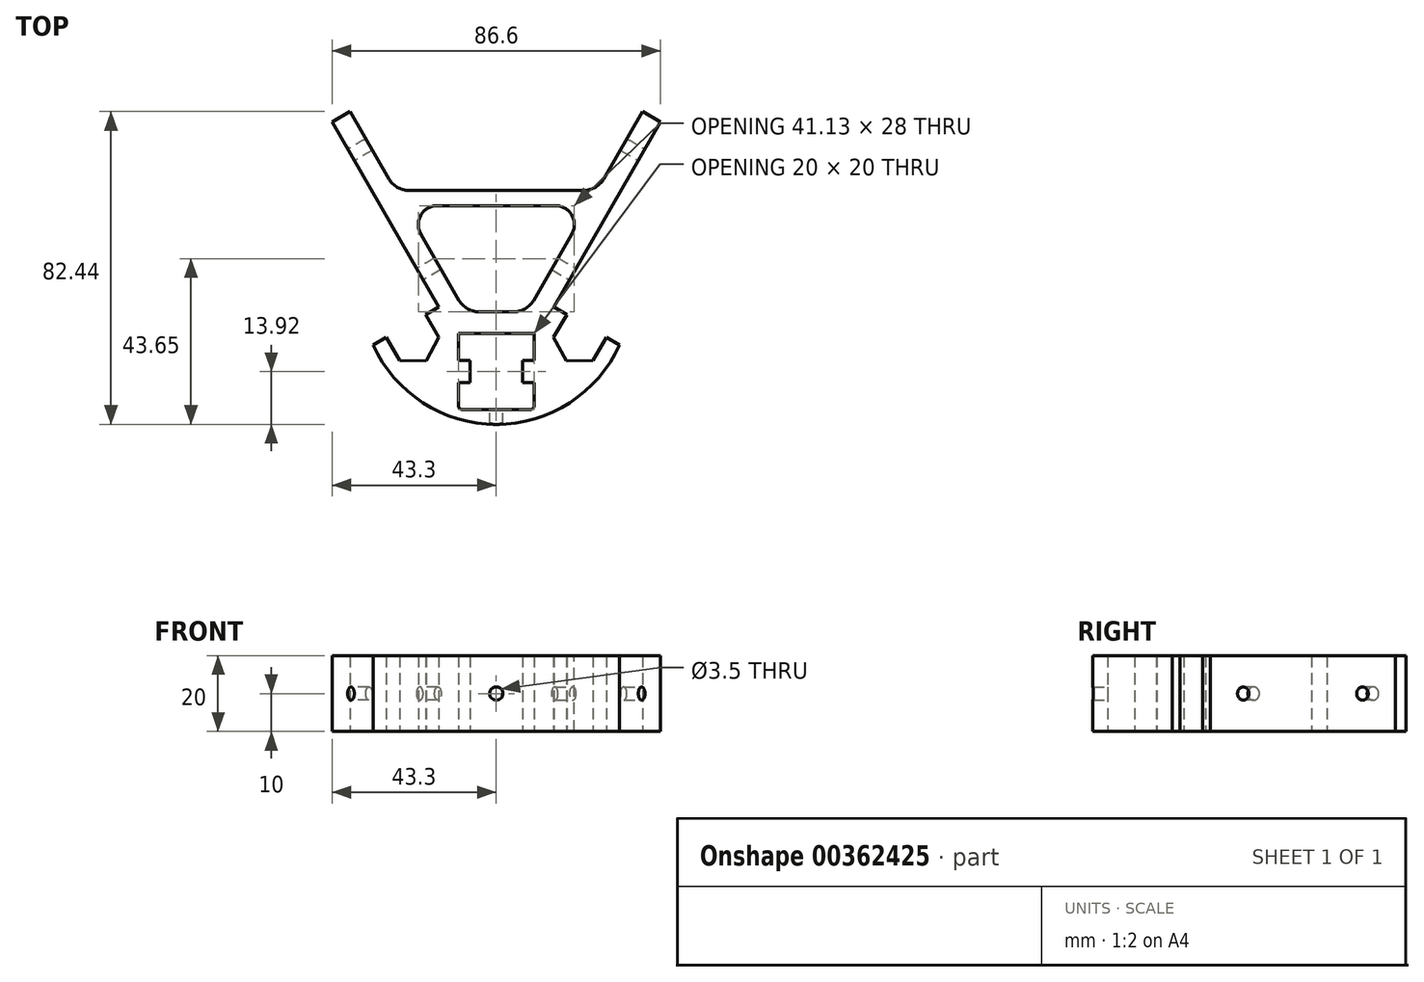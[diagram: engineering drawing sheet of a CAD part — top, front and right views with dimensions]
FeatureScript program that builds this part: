
annotation { "Feature Type Name" : "Feature", "Feature Type Description" : "" }
export const myFeature = defineFeature(function(context is Context, id is Id, definition is map)
    precondition{}
    {
        {
            var Q0;
            Q0=qCreatedBy(makeId("Top.planeOp"),FACE);
            var sketch = newSketch(context, id + "F0", { "sketchPlane" : qUnion([Q0])});
            skLineSegment(sketch, "E0", {"start": v(0, 0) * mm, "end": v(32.48, 0) * mm});
            skLineSegment(sketch, "E1", {"start": v(0, 0) * mm, "end": v(-32.48, 0) * mm});
            skArc(sketch, "E2", {"start": v(-32.48, 0) * mm, "mid": v(0, -20.94) * mm, "end": v(32.48, 0) * mm});
            skLineSegment(sketch, "E3", {"start": v(-32.48, 0) * mm, "end": v(-15.15, 10) * mm});
            skLineSegment(sketch, "E4", {"start": v(32.48, 0) * mm, "end": v(15.15, 10) * mm});
            skLineSegment(sketch, "E5", {"start": v(15.15, 10) * mm, "end": v(43.3, 58.75) * mm});
            skLineSegment(sketch, "E6", {"start": v(-15.15, 10) * mm, "end": v(-43.3, 58.75) * mm});
            skLineSegment(sketch, "E7", {"start": v(38.54, 61.5) * mm, "end": v(43.3, 58.75) * mm});
            skLineSegment(sketch, "E8.bottom", {"start": v(10, -17.02) * mm, "end": v(-10, -17.02) * mm});
            skLineSegment(sketch, "E8.top", {"start": v(10, 2.98) * mm, "end": v(-10, 2.98) * mm});
            skLineSegment(sketch, "E8.left", {"start": v(10, -17.02) * mm, "end": v(10, 2.98) * mm});
            skLineSegment(sketch, "E8.right", {"start": v(-10, -17.02) * mm, "end": v(-10, 2.98) * mm});
            skPoint(sketch, "E8.middle", {"position": v(0, -7.02) * mm});
            skLineSegment(sketch, "E9", {"start": v(-98.14, 8.7) * mm, "end": v(40.87, 8.7) * mm});
            skLineSegment(sketch, "E10", {"start": v(-43.3, 58.75) * mm, "end": v(-38.54, 61.5) * mm});
            skLineSegment(sketch, "E11", {"start": v(-38.54, 61.5) * mm, "end": v(-8.06, 8.7) * mm});
            skLineSegment(sketch, "E12", {"start": v(38.54, 61.5) * mm, "end": v(8.06, 8.7) * mm});
            skLineSegment(sketch, "E13", {"start": v(-98.14, 36.7) * mm, "end": v(34.35, 36.7) * mm});
            skLineSegment(sketch, "E14", {"start": v(-98.39, 40.7) * mm, "end": v(36.56, 40.7) * mm});
            skLineSegment(sketch, "E15.bottom", {"start": v(-10, -7.02) * mm, "end": v(-6.9, -7.02) * mm});
            skLineSegment(sketch, "E15.top", {"start": v(-10, -4.12) * mm, "end": v(-6.9, -4.12) * mm});
            skLineSegment(sketch, "E15.left", {"start": v(-10, -7.02) * mm, "end": v(-10, -4.12) * mm});
            skLineSegment(sketch, "E15.right", {"start": v(-6.9, -7.02) * mm, "end": v(-6.9, -4.12) * mm});
            skLineSegment(sketch, "E16.top", {"start": v(-10, -9.92) * mm, "end": v(-6.9, -9.92) * mm});
            skLineSegment(sketch, "E16.left", {"start": v(-10, -7.02) * mm, "end": v(-10, -9.92) * mm});
            skLineSegment(sketch, "E16.right", {"start": v(-6.9, -7.02) * mm, "end": v(-6.9, -9.92) * mm});
            skLineSegment(sketch, "E17.1.0", {"start": v(10, 2.98) * mm, "end": v(10, -17.02) * mm});
            skLineSegment(sketch, "E17.1.1", {"start": v(2.9, -17.02) * mm, "end": v(2.9, -13.92) * mm});
            skLineSegment(sketch, "E17.1.2", {"start": v(0, -17.02) * mm, "end": v(0, -13.92) * mm});
            skLineSegment(sketch, "E17.1.3", {"start": v(-2.9, -17.02) * mm, "end": v(-2.9, -13.92) * mm});
            skLineSegment(sketch, "E17.1.4", {"start": v(0, -13.92) * mm, "end": v(-2.9, -13.92) * mm});
            skLineSegment(sketch, "E17.1.5", {"start": v(0, -13.92) * mm, "end": v(2.9, -13.92) * mm});
            skLineSegment(sketch, "E17.2.0", {"start": v(-10, 2.98) * mm, "end": v(10, 2.98) * mm});
            skLineSegment(sketch, "E17.2.1", {"start": v(10, -4.12) * mm, "end": v(6.9, -4.12) * mm});
            skLineSegment(sketch, "E17.2.2", {"start": v(10, -7.02) * mm, "end": v(6.9, -7.02) * mm});
            skLineSegment(sketch, "E17.2.3", {"start": v(10, -9.92) * mm, "end": v(6.9, -9.92) * mm});
            skLineSegment(sketch, "E17.2.4", {"start": v(6.9, -7.02) * mm, "end": v(6.9, -9.92) * mm});
            skLineSegment(sketch, "E17.2.5", {"start": v(6.9, -7.02) * mm, "end": v(6.9, -4.12) * mm});
            skLineSegment(sketch, "E17.3.1", {"start": v(-2.9, 2.98) * mm, "end": v(-2.9, -0.12) * mm});
            skLineSegment(sketch, "E17.3.2", {"start": v(0, 2.98) * mm, "end": v(0, -0.12) * mm});
            skLineSegment(sketch, "E17.3.3", {"start": v(2.9, 2.98) * mm, "end": v(2.9, -0.12) * mm});
            skLineSegment(sketch, "E17.3.4", {"start": v(0, -0.12) * mm, "end": v(2.9, -0.12) * mm});
            skLineSegment(sketch, "E17.3.5", {"start": v(0, -0.12) * mm, "end": v(-2.9, -0.12) * mm});
            skLineSegment(sketch, "E18", {"start": v(18.62, 8) * mm, "end": v(15.12, 1.94) * mm});
            skLineSegment(sketch, "E19", {"start": v(29.01, 2) * mm, "end": v(25.51, -4.06) * mm});
            skPoint(sketch, "E20", {"position": v(23.81, 5) * mm});
            skLineSegment(sketch, "E21", {"start": v(15.12, 1.94) * mm, "end": v(18.51, -4.18) * mm});
            skLineSegment(sketch, "E22", {"start": v(25.51, -4.06) * mm, "end": v(18.51, -4.18) * mm});
            skLineSegment(sketch, "E23.MirrorCS", {"start": v(-18.62, 8) * mm, "end": v(-15.12, 1.94) * mm});
            skLineSegment(sketch, "E24.MirrorCS", {"start": v(-15.12, 1.94) * mm, "end": v(-18.51, -4.18) * mm});
            skLineSegment(sketch, "E25.MirrorCS", {"start": v(-25.51, -4.06) * mm, "end": v(-18.51, -4.18) * mm});
            skLineSegment(sketch, "E26.MirrorCS", {"start": v(-29.01, 2) * mm, "end": v(-25.51, -4.06) * mm});
            skSolve(sketch);
        }
        {
            var Q0;
            {var subQ5=sQuery(id+"F0.wireOp",EDGE,"E6");var subQ6=sQuery(id+"F0.wireOp",EDGE,"E3");var subQ7=makeQuery(id+"F0.imprint","INTERSECT",VERTEX,{"derivedFrom":[subQ6,subQ5]});Q0=makeQuery(id+"F0.imprint","IMPRINT",FACE,{"disambiguationData":[TD([[makeQuery(id+"F0.imprint","IMPRINT",EDGE,{"disambiguationData":[TD([[subQ7,1.0]])],"derivedFrom":subQ6}),-1.0]])]});}
            var Q1;
            {var subQ3=sQuery(id+"F0.wireOp",EDGE,"E4");var subQ7=sQuery(id+"F0.wireOp",EDGE,"E5");var subQ8=makeQuery(id+"F0.imprint","INTERSECT",VERTEX,{"derivedFrom":[subQ3,subQ7]});Q1=makeQuery(id+"F0.imprint","IMPRINT",FACE,{"disambiguationData":[TD([[makeQuery(id+"F0.imprint","IMPRINT",EDGE,{"disambiguationData":[TD([[subQ8,1.0]])],"derivedFrom":subQ3}),1.0]])]});}
            var Q2;
            {var subQ0=sQuery(id+"F0.wireOp",EDGE,"E10");Q2=makeQuery(id+"F0.imprint","IMPRINT",FACE,{"disambiguationData":[TD([[makeQuery(id+"F0.imprint","IMPRINT",EDGE,{"derivedFrom":subQ0}),-1.0]])]});}
            var Q3;
            {var subQ0=sQuery(id+"F0.wireOp",EDGE,"E13");var subQ1=sQuery(id+"F0.wireOp",EDGE,"E6");var subQ2=makeQuery(id+"F0.imprint","INTERSECT",VERTEX,{"derivedFrom":[subQ1,subQ0]});Q3=makeQuery(id+"F0.imprint","IMPRINT",FACE,{"disambiguationData":[TD([[makeQuery(id+"F0.imprint","IMPRINT",EDGE,{"disambiguationData":[TD([[subQ2,-1.0]])],"derivedFrom":subQ1}),-1.0]])]});}
            var Q4;
            {var subQ0=sQuery(id+"F0.wireOp",EDGE,"E13");var subQ1=sQuery(id+"F0.wireOp",EDGE,"E5");var subQ2=makeQuery(id+"F0.imprint","INTERSECT",VERTEX,{"derivedFrom":[subQ1,subQ0]});Q4=makeQuery(id+"F0.imprint","IMPRINT",FACE,{"disambiguationData":[TD([[makeQuery(id+"F0.imprint","IMPRINT",EDGE,{"disambiguationData":[TD([[subQ2,-1.0]])],"derivedFrom":subQ1}),1.0]])]});}
            var Q5;
            {var subQ0=sQuery(id+"F0.wireOp",EDGE,"E7");Q5=makeQuery(id+"F0.imprint","IMPRINT",FACE,{"disambiguationData":[TD([[makeQuery(id+"F0.imprint","IMPRINT",EDGE,{"derivedFrom":subQ0}),-1.0]])]});}
            var Q6;
            {var subQ19=sQuery(id+"F0.wireOp",EDGE,"E2");Q6=makeQuery(id+"F0.imprint","IMPRINT",FACE,{"disambiguationData":[TD([[makeQuery(id+"F0.imprint","IMPRINT",EDGE,{"derivedFrom":subQ19}),1.0]])]});}
            var Q7;
            {var subQ20=sQuery(id+"F0.wireOp",EDGE,"E18");Q7=makeQuery(id+"F0.imprint","IMPRINT",FACE,{"disambiguationData":[TD([[makeQuery(id+"F0.imprint","IMPRINT",EDGE,{"derivedFrom":subQ20}),-1.0]])]});}
            var Q8;
            {var subQ0=sQuery(id+"F0.wireOp",EDGE,"E15.top");Q8=makeQuery(id+"F0.imprint","IMPRINT",FACE,{"disambiguationData":[TD([[makeQuery(id+"F0.imprint","IMPRINT",EDGE,{"derivedFrom":subQ0}),-1.0]])]});}
            var Q9;
            {var subQ0=sQuery(id+"F0.wireOp",EDGE,"E15.bottom");Q9=makeQuery(id+"F0.imprint","IMPRINT",FACE,{"disambiguationData":[TD([[makeQuery(id+"F0.imprint","IMPRINT",EDGE,{"derivedFrom":subQ0}),-1.0]])]});}
            var Q10;
            {var subQ0=sQuery(id+"F0.wireOp",EDGE,"E17.2.2");Q10=makeQuery(id+"F0.imprint","IMPRINT",FACE,{"disambiguationData":[TD([[makeQuery(id+"F0.imprint","IMPRINT",EDGE,{"derivedFrom":subQ0}),1.0]])]});}
            var Q11;
            {var subQ0=sQuery(id+"F0.wireOp",EDGE,"E17.2.1");Q11=makeQuery(id+"F0.imprint","IMPRINT",FACE,{"disambiguationData":[TD([[makeQuery(id+"F0.imprint","IMPRINT",EDGE,{"derivedFrom":subQ0}),1.0]])]});}
            var Q12;
            {var subQ0=sQuery(id+"F0.wireOp",EDGE,"E17.3.2");var subQ5=sQuery(id+"F0.wireOp",EDGE,"E17.2.0");var subQ6=makeQuery(id+"F0.imprint","INTERSECT",VERTEX,{"derivedFrom":[subQ5,subQ0]});Q12=makeQuery(id+"F0.imprint","IMPRINT",FACE,{"disambiguationData":[TD([[makeQuery(id+"F0.imprint","IMPRINT",EDGE,{"disambiguationData":[TD([[subQ6,-1.0]])],"derivedFrom":subQ5}),-1.0]])]});}
            var Q13;
            {var subQ3=sQuery(id+"F0.wireOp",EDGE,"E17.3.1");var subQ5=sQuery(id+"F0.wireOp",EDGE,"E17.2.0");var subQ6=makeQuery(id+"F0.imprint","INTERSECT",VERTEX,{"derivedFrom":[subQ5,subQ3]});Q13=makeQuery(id+"F0.imprint","IMPRINT",FACE,{"disambiguationData":[TD([[makeQuery(id+"F0.imprint","IMPRINT",EDGE,{"disambiguationData":[TD([[subQ6,-1.0]])],"derivedFrom":subQ5}),-1.0]])]});}
            var Q14;
            {var subQ0=sQuery(id+"F0.wireOp",EDGE,"E3");var subQ3=sQuery(id+"F0.wireOp",EDGE,"E26.MirrorCS");var subQ5=makeQuery(id+"F0.imprint","INTERSECT",VERTEX,{"derivedFrom":[subQ0,subQ3]});Q14=makeQuery(id+"F0.imprint","IMPRINT",FACE,{"disambiguationData":[TD([[makeQuery(id+"F0.imprint","IMPRINT",EDGE,{"disambiguationData":[TD([[subQ5,-1.0]])],"derivedFrom":subQ3}),-1.0]])]});}
            var Q15;
            {var subQ0=sQuery(id+"F0.wireOp",EDGE,"E4");var subQ3=sQuery(id+"F0.wireOp",EDGE,"E19");var subQ5=makeQuery(id+"F0.imprint","INTERSECT",VERTEX,{"derivedFrom":[subQ0,subQ3]});Q15=makeQuery(id+"F0.imprint","IMPRINT",FACE,{"disambiguationData":[TD([[makeQuery(id+"F0.imprint","IMPRINT",EDGE,{"disambiguationData":[TD([[subQ5,-1.0]])],"derivedFrom":subQ3}),1.0]])]});}
            var Q16;
            {var subQ0=sQuery(id+"F0.wireOp",EDGE,"E14");var subQ1=sQuery(id+"F0.wireOp",EDGE,"E11");var subQ2=makeQuery(id+"F0.imprint","INTERSECT",VERTEX,{"derivedFrom":[subQ1,subQ0]});Q16=makeQuery(id+"F0.imprint","IMPRINT",FACE,{"disambiguationData":[TD([[makeQuery(id+"F0.imprint","IMPRINT",EDGE,{"disambiguationData":[TD([[subQ2,-1.0]])],"derivedFrom":subQ1}),1.0]])]});}
            extrude(context, id + "F1", {"entities" : qUnion([Q0, Q1, Q2, Q3, Q4, Q5, Q6, Q7, Q8, Q9, Q10, Q11, Q12, Q13, Q14, Q15, Q16]), "depth" : 20 * mm});
        }
        {
            var Q0;
            Q0=makeQuery(id+"F1.opExtrude","SWEPT_EDGE",EDGE,{"disambiguationData":[OSD([sQuery(id+"F0.wireOp",EDGE,"E8.bottom"),sQuery(id+"F0.wireOp",EDGE,"E17.1.0")])]});
            var Q1;
            Q1=makeQuery(id+"F1.opExtrude","SWEPT_EDGE",EDGE,{"disambiguationData":[OSD([sQuery(id+"F0.wireOp",EDGE,"E8.bottom"),sQuery(id+"F0.wireOp",EDGE,"E8.right")])]});
            var Q2;
            Q2=makeQuery(id+"F1.opExtrude","SWEPT_EDGE",EDGE,{"disambiguationData":[OSD([sQuery(id+"F0.wireOp",EDGE,"E17.2.0"),sQuery(id+"F0.wireOp",EDGE,"E8.right")])]});
            var Q3;
            Q3=makeQuery(id+"F1.opExtrude","SWEPT_EDGE",EDGE,{"disambiguationData":[OSD([sQuery(id+"F0.wireOp",EDGE,"E17.1.0"),sQuery(id+"F0.wireOp",EDGE,"E17.2.0")])]});
            fillet(context, id + "F2", {"entities" : qUnion([Q0, Q1, Q2, Q3]), "radius" : 1 * mm, "tangentPropagation" : true, "allowEdgeOverflow" : false});
        }
        {
            var Q0;
            Q0=makeQuery(id+"F1.opExtrude","SWEPT_EDGE",EDGE,{"disambiguationData":[OSD([sQuery(id+"F0.wireOp",EDGE,"E9"),sQuery(id+"F0.wireOp",EDGE,"E11")])]});
            var Q1;
            Q1=makeQuery(id+"F1.opExtrude","SWEPT_EDGE",EDGE,{"disambiguationData":[OSD([sQuery(id+"F0.wireOp",EDGE,"E9"),sQuery(id+"F0.wireOp",EDGE,"E12")])]});
            var Q2;
            Q2=makeQuery(id+"F1.opExtrude","SWEPT_EDGE",EDGE,{"disambiguationData":[OSD([sQuery(id+"F0.wireOp",EDGE,"E12"),sQuery(id+"F0.wireOp",EDGE,"E14")])]});
            var Q3;
            Q3=makeQuery(id+"F1.opExtrude","SWEPT_EDGE",EDGE,{"disambiguationData":[OSD([sQuery(id+"F0.wireOp",EDGE,"E11"),sQuery(id+"F0.wireOp",EDGE,"E14")])]});
            fillet(context, id + "F3", {"entities" : qUnion([Q0, Q1, Q2, Q3]), "radius" : 6 * mm, "tangentPropagation" : true, "allowEdgeOverflow" : false});
        }
        {
            var Q0;
            Q0=makeQuery(id+"F1.opExtrude","SWEPT_FACE",FACE,{"disambiguationData":[OSD([sQuery(id+"F0.wireOp",EDGE,"E5")])]});
            var sketch = newSketch(context, id + "F4", { "sketchPlane" : qUnion([Q0])});
            skCircle(sketch, "E27", {"center": v(26.24, 10) * mm, "radius": 1.75 * mm});
            skCircle(sketch, "E28", {"center": v(62.53, 10) * mm, "radius": 1.75 * mm});
            skSolve(sketch);
        }
        {
            var Q0;
            Q0 = qSketchRegion(id + "F4", true);
            var Q1;
            {var subQ0=sQuery(id+"F0.wireOp",EDGE,"E12");Q1=makeQuery(id+"F1.opExtrude","SWEPT_FACE",FACE,{"disambiguationData":[OSD([subQ0]),TDD([makeQuery(id+"F0.imprint","IMPRINT",EDGE,{"disambiguationData":[TD([[makeQuery(id+"F0.imprint","INTERSECT",VERTEX,{"derivedFrom":[sQuery(id+"F0.wireOp",EDGE,"E9"),subQ0]}),1.0]])],"derivedFrom":subQ0})])]});}
            extrude(context, id + "F5", {"entities" : qUnion([Q0]), "operationType" : NewBodyOperationType.REMOVE, "endBound" : BoundingType.UP_TO_SURFACE, "oppositeDirection" : true, "endBoundEntityFace" : qUnion([Q1]), "depth" : 25 * mm});
        }
        {
            var Q0;
            Q0=makeQuery(id+"F1.opExtrude","SWEPT_FACE",FACE,{"disambiguationData":[OSD([sQuery(id+"F0.wireOp",EDGE,"E8.bottom")])]});
            var sketch = newSketch(context, id + "F6", { "sketchPlane" : qUnion([Q0])});
            skCircle(sketch, "E29", {"center": v(0, 10) * mm, "radius": 1.75 * mm});
            skSolve(sketch);
        }
        {
            var Q0;
            Q0=makeQuery(id+"F6.imprint","IMPRINT",FACE,{"disambiguationData":[TD([[makeQuery(id+"F6.imprint","IMPRINT",EDGE,{"derivedFrom":sQuery(id+"F6.wireOp",EDGE,"E29")}),1.0]])]});
            var Q1;
            Q1=makeQuery(id+"F1.opExtrude","SWEPT_FACE",FACE,{"disambiguationData":[OSD([sQuery(id+"F0.wireOp",EDGE,"E2")])]});
            extrude(context, id + "F7", {"entities" : qUnion([Q0]), "operationType" : NewBodyOperationType.REMOVE, "endBound" : BoundingType.UP_TO_SURFACE, "oppositeDirection" : true, "endBoundEntityFace" : qUnion([Q1]), "depth" : 25 * mm});
        }
        {
            var Q0;
            Q0=makeQuery(id+"F1.opExtrude","SWEPT_BODY",BODY,{"disambiguationData":[OSD([sQuery(id+"F0.wireOp",EDGE,"E0"),sQuery(id+"F0.wireOp",EDGE,"E1"),sQuery(id+"F0.wireOp",EDGE,"E2"),sQuery(id+"F0.wireOp",EDGE,"E3"),sQuery(id+"F0.wireOp",EDGE,"E4"),sQuery(id+"F0.wireOp",EDGE,"E5"),sQuery(id+"F0.wireOp",EDGE,"E6"),sQuery(id+"F0.wireOp",EDGE,"E7"),sQuery(id+"F0.wireOp",EDGE,"E8.bottom"),sQuery(id+"F0.wireOp",EDGE,"E9"),sQuery(id+"F0.wireOp",EDGE,"E10"),sQuery(id+"F0.wireOp",EDGE,"E11"),sQuery(id+"F0.wireOp",EDGE,"E12"),sQuery(id+"F0.wireOp",EDGE,"E13"),sQuery(id+"F0.wireOp",EDGE,"E14"),sQuery(id+"F0.wireOp",EDGE,"E15.top"),sQuery(id+"F0.wireOp",EDGE,"E15.right"),sQuery(id+"F0.wireOp",EDGE,"E16.top"),sQuery(id+"F0.wireOp",EDGE,"E16.right"),sQuery(id+"F0.wireOp",EDGE,"E17.1.0"),sQuery(id+"F0.wireOp",EDGE,"E17.2.0"),sQuery(id+"F0.wireOp",EDGE,"E17.2.1"),sQuery(id+"F0.wireOp",EDGE,"E17.2.3"),sQuery(id+"F0.wireOp",EDGE,"E17.2.4"),sQuery(id+"F0.wireOp",EDGE,"E17.2.5"),sQuery(id+"F0.wireOp",EDGE,"E8.right"),sQuery(id+"F0.wireOp",EDGE,"E17.3.1"),sQuery(id+"F0.wireOp",EDGE,"E17.3.3"),sQuery(id+"F0.wireOp",EDGE,"E18"),sQuery(id+"F0.wireOp",EDGE,"E19"),sQuery(id+"F0.wireOp",EDGE,"E21"),sQuery(id+"F0.wireOp",EDGE,"E22"),sQuery(id+"F0.wireOp",EDGE,"E23.MirrorCS"),sQuery(id+"F0.wireOp",EDGE,"E24.MirrorCS"),sQuery(id+"F0.wireOp",EDGE,"E25.MirrorCS"),sQuery(id+"F0.wireOp",EDGE,"E26.MirrorCS")])]});
            transform(context, id + "F8", {"entities" : qUnion([Q0]), "transformType" : TransformType.TRANSLATION_3D, "dx" : 0 * mm, "dy" : 7.02 * mm, "dz" : 0 * mm, "makeCopy" : false});
        }
        {
            var Q0;
            Q0=makeQuery(id+"F1.opExtrude","SWEPT_BODY",BODY,{"disambiguationData":[OSD([sQuery(id+"F0.wireOp",EDGE,"E0"),sQuery(id+"F0.wireOp",EDGE,"E1"),sQuery(id+"F0.wireOp",EDGE,"E2"),sQuery(id+"F0.wireOp",EDGE,"E3"),sQuery(id+"F0.wireOp",EDGE,"E4"),sQuery(id+"F0.wireOp",EDGE,"E5"),sQuery(id+"F0.wireOp",EDGE,"E6"),sQuery(id+"F0.wireOp",EDGE,"E7"),sQuery(id+"F0.wireOp",EDGE,"E8.bottom"),sQuery(id+"F0.wireOp",EDGE,"E9"),sQuery(id+"F0.wireOp",EDGE,"E10"),sQuery(id+"F0.wireOp",EDGE,"E11"),sQuery(id+"F0.wireOp",EDGE,"E12"),sQuery(id+"F0.wireOp",EDGE,"E13"),sQuery(id+"F0.wireOp",EDGE,"E14"),sQuery(id+"F0.wireOp",EDGE,"E15.top"),sQuery(id+"F0.wireOp",EDGE,"E15.right"),sQuery(id+"F0.wireOp",EDGE,"E16.top"),sQuery(id+"F0.wireOp",EDGE,"E16.right"),sQuery(id+"F0.wireOp",EDGE,"E17.1.0"),sQuery(id+"F0.wireOp",EDGE,"E17.2.0"),sQuery(id+"F0.wireOp",EDGE,"E17.2.1"),sQuery(id+"F0.wireOp",EDGE,"E17.2.3"),sQuery(id+"F0.wireOp",EDGE,"E17.2.4"),sQuery(id+"F0.wireOp",EDGE,"E17.2.5"),sQuery(id+"F0.wireOp",EDGE,"E8.right"),sQuery(id+"F0.wireOp",EDGE,"E17.3.1"),sQuery(id+"F0.wireOp",EDGE,"E17.3.3"),sQuery(id+"F0.wireOp",EDGE,"E18"),sQuery(id+"F0.wireOp",EDGE,"E19"),sQuery(id+"F0.wireOp",EDGE,"E21"),sQuery(id+"F0.wireOp",EDGE,"E22"),sQuery(id+"F0.wireOp",EDGE,"E23.MirrorCS"),sQuery(id+"F0.wireOp",EDGE,"E24.MirrorCS"),sQuery(id+"F0.wireOp",EDGE,"E25.MirrorCS"),sQuery(id+"F0.wireOp",EDGE,"E26.MirrorCS")])]});
            var Q1;
            Q1=qCreatedBy(makeId("Right.planeOp"),FACE);
            mirror(context, id + "F9", {"operationType" : NewBodyOperationType.INTERSECT, "entities" : qUnion([Q0]), "mirrorPlane" : qUnion([Q1])});
        }
        {
            var Q0;
            Q0=makeQuery(id+"F1.opExtrude","SWEPT_EDGE",EDGE,{"disambiguationData":[OSD([sQuery(id+"F0.wireOp",EDGE,"E12"),sQuery(id+"F0.wireOp",EDGE,"E13")])]});
            var Q1;
            Q1=makeQuery(id+"F1.opExtrude","SWEPT_EDGE",EDGE,{"disambiguationData":[OSD([sQuery(id+"F0.wireOp",EDGE,"E11"),sQuery(id+"F0.wireOp",EDGE,"E13")])]});
            fillet(context, id + "F10", {"entities" : qUnion([Q0, Q1]), "radius" : 5 * mm, "tangentPropagation" : true, "allowEdgeOverflow" : false});
        }
    });
